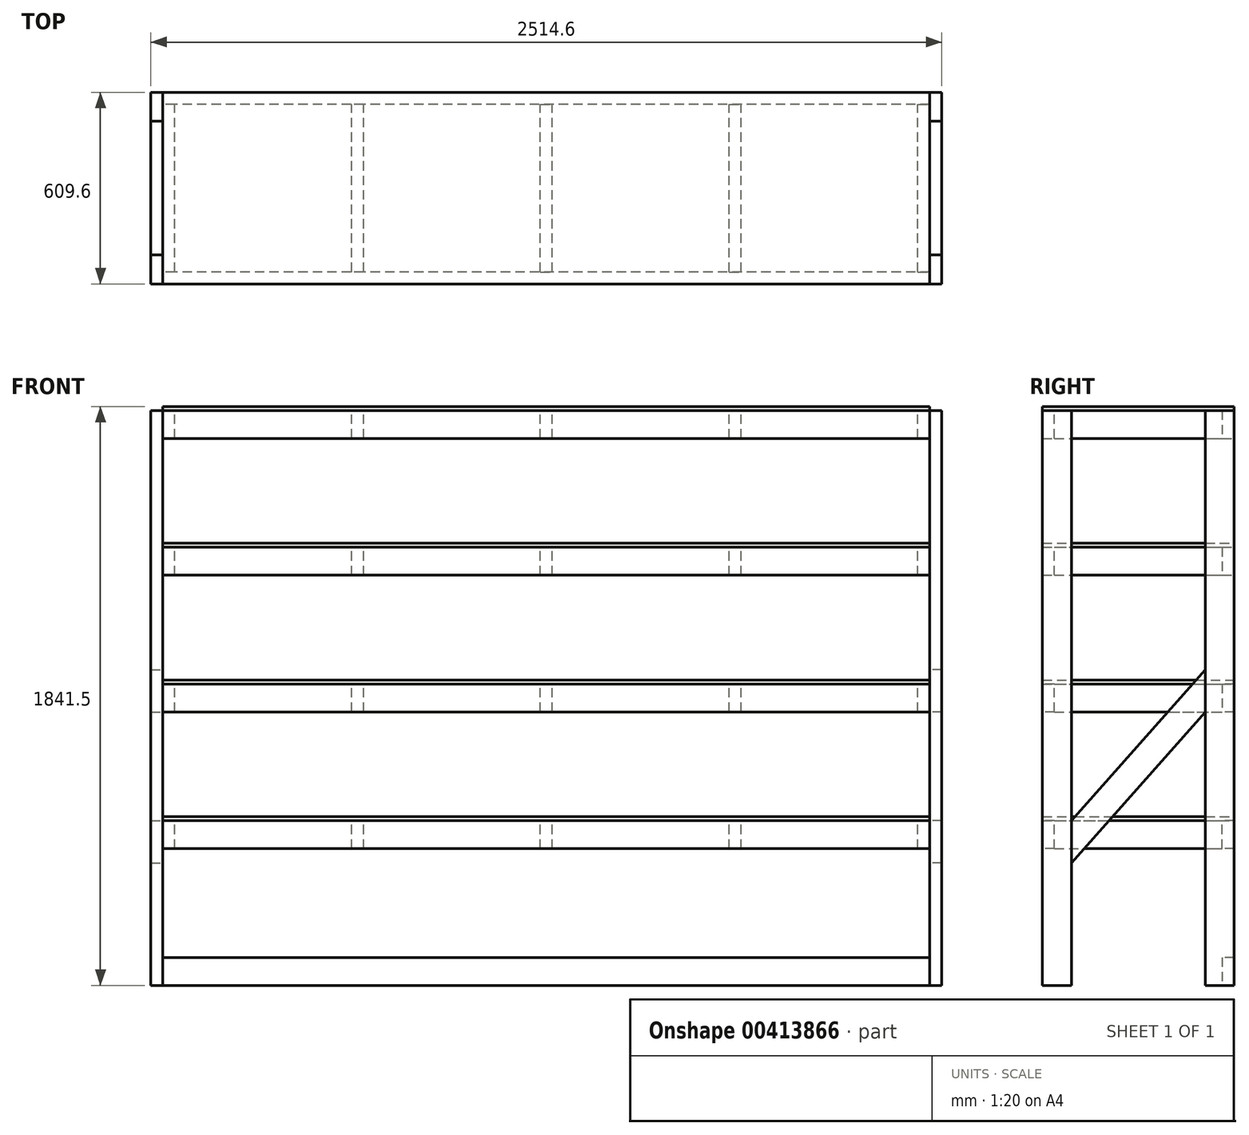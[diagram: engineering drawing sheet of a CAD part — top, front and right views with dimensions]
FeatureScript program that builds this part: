
annotation { "Feature Type Name" : "Feature", "Feature Type Description" : "" }
export const myFeature = defineFeature(function(context is Context, id is Id, definition is map)
    precondition{}
    {
        {
            var Q0;
            Q0=qCreatedBy(makeId("Top.planeOp"),FACE);
            var sketch = newSketch(context, id + "F0", { "sketchPlane" : qUnion([Q0])});
            skLineSegment(sketch, "E0.bottom", {"start": v(1219.2, 304.8) * mm, "end": v(-1219.2, 304.8) * mm, "construction": true});
            skLineSegment(sketch, "E0.top", {"start": v(1219.2, -304.8) * mm, "end": v(-1219.2, -304.8) * mm, "construction": true});
            skLineSegment(sketch, "E0.left", {"start": v(1219.2, 304.8) * mm, "end": v(1219.2, -304.8) * mm, "construction": true});
            skLineSegment(sketch, "E0.right", {"start": v(-1219.2, 304.8) * mm, "end": v(-1219.2, -304.8) * mm, "construction": true});
            skPoint(sketch, "E0.middle", {"position": v(0, 0) * mm});
            skSolve(sketch);
        }
        {
            var Q0;
            Q0=qCreatedBy(makeId("Top.planeOp"),FACE);
            var sketch = newSketch(context, id + "F1", { "sketchPlane" : qUnion([Q0])});
            skLineSegment(sketch, "E1.bottom", {"start": v(-1257.3, 304.8) * mm, "end": v(-1219.2, 304.8) * mm});
            skLineSegment(sketch, "E1.top", {"start": v(-1257.3, 212.72) * mm, "end": v(-1219.2, 212.72) * mm});
            skLineSegment(sketch, "E1.left", {"start": v(-1257.3, 304.8) * mm, "end": v(-1257.3, 212.72) * mm});
            skLineSegment(sketch, "E1.right", {"start": v(-1219.2, 304.8) * mm, "end": v(-1219.2, 212.72) * mm});
            skLineSegment(sketch, "E2.bottom", {"start": v(-1257.3, -304.8) * mm, "end": v(-1219.2, -304.8) * mm});
            skLineSegment(sketch, "E2.top", {"start": v(-1257.3, -212.73) * mm, "end": v(-1219.2, -212.73) * mm});
            skLineSegment(sketch, "E2.left", {"start": v(-1257.3, -304.8) * mm, "end": v(-1257.3, -212.73) * mm});
            skLineSegment(sketch, "E2.right", {"start": v(-1219.2, -304.8) * mm, "end": v(-1219.2, -212.73) * mm});
            skLineSegment(sketch, "E3.bottom", {"start": v(1257.3, -304.8) * mm, "end": v(1219.2, -304.8) * mm});
            skLineSegment(sketch, "E3.top", {"start": v(1257.3, -212.73) * mm, "end": v(1219.2, -212.73) * mm});
            skLineSegment(sketch, "E3.left", {"start": v(1257.3, -304.8) * mm, "end": v(1257.3, -212.73) * mm});
            skLineSegment(sketch, "E3.right", {"start": v(1219.2, -304.8) * mm, "end": v(1219.2, -212.73) * mm});
            skLineSegment(sketch, "E4.bottom", {"start": v(1257.3, 304.8) * mm, "end": v(1219.2, 304.8) * mm});
            skLineSegment(sketch, "E4.top", {"start": v(1257.3, 212.72) * mm, "end": v(1219.2, 212.72) * mm});
            skLineSegment(sketch, "E4.left", {"start": v(1257.3, 304.8) * mm, "end": v(1257.3, 212.72) * mm});
            skLineSegment(sketch, "E4.right", {"start": v(1219.2, 304.8) * mm, "end": v(1219.2, 212.72) * mm});
            skSolve(sketch);
        }
        {
            var Q0;
            Q0=makeQuery(id+"F1.imprint","IMPRINT",FACE,{"disambiguationData":[TD([[makeQuery(id+"F1.imprint","IMPRINT",EDGE,{"derivedFrom":sQuery(id+"F1.wireOp",EDGE,"E2.bottom")}),1.0]])]});
            var Q1;
            Q1=makeQuery(id+"F1.imprint","IMPRINT",FACE,{"disambiguationData":[TD([[makeQuery(id+"F1.imprint","IMPRINT",EDGE,{"derivedFrom":sQuery(id+"F1.wireOp",EDGE,"E1.bottom")}),-1.0]])]});
            var Q2;
            Q2=makeQuery(id+"F1.imprint","IMPRINT",FACE,{"disambiguationData":[TD([[makeQuery(id+"F1.imprint","IMPRINT",EDGE,{"derivedFrom":sQuery(id+"F1.wireOp",EDGE,"E3.bottom")}),-1.0]])]});
            var Q3;
            Q3=makeQuery(id+"F1.imprint","IMPRINT",FACE,{"disambiguationData":[TD([[makeQuery(id+"F1.imprint","IMPRINT",EDGE,{"derivedFrom":sQuery(id+"F1.wireOp",EDGE,"E4.bottom")}),1.0]])]});
            extrude(context, id + "F2", {"entities" : qUnion([Q0, Q1, Q2, Q3]), "depth" : 1828.8 * mm});
        }
        {
            var Q0;
            Q0=qCreatedBy(makeId("Right.planeOp"),FACE);
            var sketch = newSketch(context, id + "F3", { "sketchPlane" : qUnion([Q0])});
            skLineSegment(sketch, "E5.bottom", {"start": v(266.7, 1828.8) * mm, "end": v(304.8, 1828.8) * mm});
            skLineSegment(sketch, "E5.top", {"start": v(266.7, 1739.9) * mm, "end": v(304.8, 1739.9) * mm});
            skLineSegment(sketch, "E5.left", {"start": v(266.7, 1828.8) * mm, "end": v(266.7, 1739.9) * mm});
            skLineSegment(sketch, "E5.right", {"start": v(304.8, 1828.8) * mm, "end": v(304.8, 1739.9) * mm});
            skLineSegment(sketch, "E6.bottom", {"start": v(266.7, 1393.83) * mm, "end": v(304.8, 1393.83) * mm});
            skLineSegment(sketch, "E6.top", {"start": v(266.7, 1304.93) * mm, "end": v(304.8, 1304.93) * mm});
            skLineSegment(sketch, "E6.left", {"start": v(266.7, 1393.83) * mm, "end": v(266.7, 1304.93) * mm});
            skLineSegment(sketch, "E6.right", {"start": v(304.8, 1393.83) * mm, "end": v(304.8, 1304.93) * mm});
            skLineSegment(sketch, "E7.bottom", {"start": v(304.8, 958.85) * mm, "end": v(266.7, 958.85) * mm});
            skLineSegment(sketch, "E7.top", {"start": v(304.8, 869.95) * mm, "end": v(266.7, 869.95) * mm});
            skLineSegment(sketch, "E7.left", {"start": v(304.8, 958.85) * mm, "end": v(304.8, 869.95) * mm});
            skLineSegment(sketch, "E7.right", {"start": v(266.7, 958.85) * mm, "end": v(266.7, 869.95) * mm});
            skLineSegment(sketch, "E8.bottom", {"start": v(304.8, 523.87) * mm, "end": v(266.7, 523.87) * mm});
            skLineSegment(sketch, "E8.top", {"start": v(304.8, 434.98) * mm, "end": v(266.7, 434.98) * mm});
            skLineSegment(sketch, "E8.left", {"start": v(304.8, 523.87) * mm, "end": v(304.8, 434.98) * mm});
            skLineSegment(sketch, "E8.right", {"start": v(266.7, 523.88) * mm, "end": v(266.7, 434.98) * mm});
            skLineSegment(sketch, "E9.bottom", {"start": v(304.8, 88.9) * mm, "end": v(266.7, 88.9) * mm});
            skLineSegment(sketch, "E9.top", {"start": v(304.8, 0) * mm, "end": v(266.7, 0) * mm});
            skLineSegment(sketch, "E9.left", {"start": v(304.8, 88.9) * mm, "end": v(304.8, 0) * mm});
            skLineSegment(sketch, "E9.right", {"start": v(266.7, 88.9) * mm, "end": v(266.7, 0) * mm});
            skLineSegment(sketch, "E10", {"start": v(266.7, 1739.9) * mm, "end": v(266.7, 1393.83) * mm, "construction": true});
            skLineSegment(sketch, "E11", {"start": v(266.7, 1304.93) * mm, "end": v(266.7, 958.85) * mm, "construction": true});
            skLineSegment(sketch, "E12", {"start": v(266.7, 869.95) * mm, "end": v(266.7, 523.87) * mm, "construction": true});
            skLineSegment(sketch, "E13", {"start": v(266.7, 434.98) * mm, "end": v(266.7, 88.9) * mm, "construction": true});
            skLineSegment(sketch, "E14.MirrorCS", {"start": v(-266.7, 1828.8) * mm, "end": v(-304.8, 1828.8) * mm});
            skLineSegment(sketch, "E15.MirrorCS", {"start": v(-266.7, 1739.9) * mm, "end": v(-304.8, 1739.9) * mm});
            skLineSegment(sketch, "E16.MirrorCS", {"start": v(-304.8, 434.98) * mm, "end": v(-266.7, 434.98) * mm});
            skLineSegment(sketch, "E17.MirrorCS", {"start": v(-304.8, 523.87) * mm, "end": v(-266.7, 523.87) * mm});
            skLineSegment(sketch, "E18.MirrorCS", {"start": v(-266.7, 1304.93) * mm, "end": v(-304.8, 1304.93) * mm});
            skLineSegment(sketch, "E19.MirrorCS", {"start": v(-266.7, 1393.83) * mm, "end": v(-304.8, 1393.83) * mm});
            skLineSegment(sketch, "E20.MirrorCS", {"start": v(-304.8, 958.85) * mm, "end": v(-266.7, 958.85) * mm});
            skLineSegment(sketch, "E21.MirrorCS", {"start": v(-304.8, 869.95) * mm, "end": v(-266.7, 869.95) * mm});
            skLineSegment(sketch, "E22.MirrorCS", {"start": v(-266.7, 523.88) * mm, "end": v(-266.7, 434.98) * mm});
            skLineSegment(sketch, "E23.MirrorCS", {"start": v(-266.7, 1828.8) * mm, "end": v(-266.7, 1739.9) * mm});
            skLineSegment(sketch, "E24.MirrorCS", {"start": v(-304.8, 523.87) * mm, "end": v(-304.8, 434.98) * mm});
            skLineSegment(sketch, "E25.MirrorCS", {"start": v(-266.7, 1304.93) * mm, "end": v(-266.7, 958.85) * mm, "construction": true});
            skLineSegment(sketch, "E26.MirrorCS", {"start": v(-266.7, 1393.83) * mm, "end": v(-266.7, 1304.93) * mm});
            skLineSegment(sketch, "E27.MirrorCS", {"start": v(-266.7, 958.85) * mm, "end": v(-266.7, 869.95) * mm});
            skLineSegment(sketch, "E28.MirrorCS", {"start": v(-266.7, 1739.9) * mm, "end": v(-266.7, 1393.83) * mm, "construction": true});
            skLineSegment(sketch, "E29.MirrorCS", {"start": v(-304.8, 958.85) * mm, "end": v(-304.8, 869.95) * mm});
            skLineSegment(sketch, "E30.MirrorCS", {"start": v(-266.7, 869.95) * mm, "end": v(-266.7, 523.87) * mm, "construction": true});
            skLineSegment(sketch, "E31.MirrorCS", {"start": v(-304.8, 1393.83) * mm, "end": v(-304.8, 1304.93) * mm});
            skLineSegment(sketch, "E32.MirrorCS", {"start": v(-304.8, 1828.8) * mm, "end": v(-304.8, 1739.9) * mm});
            skSolve(sketch);
        }
        {
            var Q0;
            Q0 = qSketchRegion(id + "F3", true);
            extrude(context, id + "F4", {"entities" : qUnion([Q0]), "endBound" : BoundingType.UP_TO_NEXT, "depth" : 25.4 * mm, "hasSecondDirection" : true, "secondDirectionBound" : SecondDirectionBoundingType.UP_TO_NEXT, "secondDirectionOppositeDirection" : true, "secondDirectionDepth" : 25.4 * mm});
        }
        {
            var Q0;
            Q0=qCreatedBy(makeId("Front.planeOp"),FACE);
            var sketch = newSketch(context, id + "F5", { "sketchPlane" : qUnion([Q0])});
            skLineSegment(sketch, "E33.bottom", {"start": v(-1219.2, 958.85) * mm, "end": v(-1181.1, 958.85) * mm});
            skLineSegment(sketch, "E33.top", {"start": v(-1219.2, 869.95) * mm, "end": v(-1181.1, 869.95) * mm});
            skLineSegment(sketch, "E33.left", {"start": v(-1219.2, 958.85) * mm, "end": v(-1219.2, 869.95) * mm});
            skLineSegment(sketch, "E33.right", {"start": v(-1181.1, 958.85) * mm, "end": v(-1181.1, 869.95) * mm});
            skLineSegment(sketch, "E34.bottom", {"start": v(-1219.2, 1393.83) * mm, "end": v(-1181.1, 1393.83) * mm});
            skLineSegment(sketch, "E34.top", {"start": v(-1219.2, 1304.93) * mm, "end": v(-1181.1, 1304.93) * mm});
            skLineSegment(sketch, "E34.left", {"start": v(-1219.2, 1393.83) * mm, "end": v(-1219.2, 1304.93) * mm});
            skLineSegment(sketch, "E34.right", {"start": v(-1181.1, 1393.83) * mm, "end": v(-1181.1, 1304.93) * mm});
            skLineSegment(sketch, "E35.bottom", {"start": v(-1219.2, 1828.8) * mm, "end": v(-1181.1, 1828.8) * mm});
            skLineSegment(sketch, "E35.top", {"start": v(-1219.2, 1739.9) * mm, "end": v(-1181.1, 1739.9) * mm});
            skLineSegment(sketch, "E35.left", {"start": v(-1219.2, 1828.8) * mm, "end": v(-1219.2, 1739.9) * mm});
            skLineSegment(sketch, "E35.right", {"start": v(-1181.1, 1828.8) * mm, "end": v(-1181.1, 1739.9) * mm});
            skLineSegment(sketch, "E36.bottom", {"start": v(-1219.2, 523.87) * mm, "end": v(-1181.1, 523.87) * mm});
            skLineSegment(sketch, "E36.top", {"start": v(-1219.2, 434.97) * mm, "end": v(-1181.1, 434.97) * mm});
            skLineSegment(sketch, "E36.left", {"start": v(-1219.2, 523.87) * mm, "end": v(-1219.2, 434.97) * mm});
            skLineSegment(sketch, "E36.right", {"start": v(-1181.1, 523.87) * mm, "end": v(-1181.1, 434.97) * mm});
            skLineSegment(sketch, "E37.bottom", {"start": v(-619.13, 1828.8) * mm, "end": v(-581.02, 1828.8) * mm});
            skLineSegment(sketch, "E37.top", {"start": v(-619.13, 1739.9) * mm, "end": v(-581.02, 1739.9) * mm});
            skLineSegment(sketch, "E37.left", {"start": v(-619.13, 1828.8) * mm, "end": v(-619.13, 1739.9) * mm});
            skLineSegment(sketch, "E37.right", {"start": v(-581.02, 1828.8) * mm, "end": v(-581.02, 1739.9) * mm});
            skLineSegment(sketch, "E38.bottom", {"start": v(-619.13, 1393.83) * mm, "end": v(-581.02, 1393.83) * mm});
            skLineSegment(sketch, "E38.top", {"start": v(-619.13, 1304.93) * mm, "end": v(-581.02, 1304.93) * mm});
            skLineSegment(sketch, "E38.left", {"start": v(-619.13, 1393.83) * mm, "end": v(-619.13, 1304.93) * mm});
            skLineSegment(sketch, "E38.right", {"start": v(-581.02, 1393.83) * mm, "end": v(-581.02, 1304.93) * mm});
            skLineSegment(sketch, "E39.bottom", {"start": v(-619.13, 958.85) * mm, "end": v(-581.02, 958.85) * mm});
            skLineSegment(sketch, "E39.top", {"start": v(-619.13, 869.95) * mm, "end": v(-581.02, 869.95) * mm});
            skLineSegment(sketch, "E39.left", {"start": v(-619.13, 958.85) * mm, "end": v(-619.13, 869.95) * mm});
            skLineSegment(sketch, "E39.right", {"start": v(-581.02, 958.85) * mm, "end": v(-581.02, 869.95) * mm});
            skLineSegment(sketch, "E40.bottom", {"start": v(-619.12, 523.87) * mm, "end": v(-581.02, 523.87) * mm});
            skLineSegment(sketch, "E40.top", {"start": v(-619.13, 434.97) * mm, "end": v(-581.02, 434.97) * mm});
            skLineSegment(sketch, "E40.left", {"start": v(-619.12, 523.87) * mm, "end": v(-619.12, 434.97) * mm});
            skLineSegment(sketch, "E40.right", {"start": v(-581.02, 523.88) * mm, "end": v(-581.02, 434.97) * mm});
            skLineSegment(sketch, "E41", {"start": v(-1181.1, 1828.8) * mm, "end": v(-619.13, 1828.8) * mm, "construction": true});
            skLineSegment(sketch, "E42", {"start": v(-1181.1, 1393.83) * mm, "end": v(-619.13, 1393.83) * mm, "construction": true});
            skLineSegment(sketch, "E43", {"start": v(-1181.1, 958.85) * mm, "end": v(-619.13, 958.85) * mm, "construction": true});
            skLineSegment(sketch, "E44", {"start": v(-1181.1, 523.87) * mm, "end": v(-619.12, 523.87) * mm, "construction": true});
            skLineSegment(sketch, "E45", {"start": v(0, 0) * mm, "end": v(0, 1828.8) * mm, "construction": true});
            skLineSegment(sketch, "E46.bottom", {"start": v(0, 1828.8) * mm, "end": v(-19.05, 1828.8) * mm});
            skLineSegment(sketch, "E46.top", {"start": v(0, 1739.9) * mm, "end": v(-19.05, 1739.9) * mm});
            skLineSegment(sketch, "E46.right", {"start": v(-19.05, 1828.8) * mm, "end": v(-19.05, 1739.9) * mm});
            skLineSegment(sketch, "E47.bottom", {"start": v(0, 1393.83) * mm, "end": v(-19.05, 1393.83) * mm});
            skLineSegment(sketch, "E47.top", {"start": v(0, 1304.93) * mm, "end": v(-19.05, 1304.93) * mm});
            skLineSegment(sketch, "E47.right", {"start": v(-19.05, 1393.83) * mm, "end": v(-19.05, 1304.93) * mm});
            skLineSegment(sketch, "E48.bottom", {"start": v(0, 958.85) * mm, "end": v(-19.05, 958.85) * mm});
            skLineSegment(sketch, "E48.top", {"start": v(0, 869.95) * mm, "end": v(-19.05, 869.95) * mm});
            skLineSegment(sketch, "E48.right", {"start": v(-19.05, 958.85) * mm, "end": v(-19.05, 869.95) * mm});
            skLineSegment(sketch, "E49.bottom", {"start": v(0, 523.87) * mm, "end": v(-19.05, 523.87) * mm});
            skLineSegment(sketch, "E49.top", {"start": v(0, 434.98) * mm, "end": v(-19.05, 434.98) * mm});
            skLineSegment(sketch, "E49.right", {"start": v(-19.05, 523.87) * mm, "end": v(-19.05, 434.98) * mm});
            skLineSegment(sketch, "E50", {"start": v(-581.02, 1828.8) * mm, "end": v(-19.05, 1828.8) * mm, "construction": true});
            skLineSegment(sketch, "E51.MirrorCS", {"start": v(0, 1739.9) * mm, "end": v(19.05, 1739.9) * mm});
            skLineSegment(sketch, "E52.MirrorCS", {"start": v(0, 1304.93) * mm, "end": v(19.05, 1304.93) * mm});
            skLineSegment(sketch, "E53.MirrorCS", {"start": v(0, 869.95) * mm, "end": v(19.05, 869.95) * mm});
            skLineSegment(sketch, "E54.MirrorCS", {"start": v(619.13, 1828.8) * mm, "end": v(581.02, 1828.8) * mm});
            skLineSegment(sketch, "E55.MirrorCS", {"start": v(0, 1828.8) * mm, "end": v(19.05, 1828.8) * mm});
            skLineSegment(sketch, "E56.MirrorCS", {"start": v(0, 1393.83) * mm, "end": v(19.05, 1393.83) * mm});
            skLineSegment(sketch, "E57.MirrorCS", {"start": v(619.13, 1304.93) * mm, "end": v(581.02, 1304.93) * mm});
            skLineSegment(sketch, "E58.MirrorCS", {"start": v(619.13, 869.95) * mm, "end": v(581.02, 869.95) * mm});
            skLineSegment(sketch, "E59.MirrorCS", {"start": v(0, 434.98) * mm, "end": v(19.05, 434.98) * mm});
            skLineSegment(sketch, "E60.MirrorCS", {"start": v(1219.2, 1304.93) * mm, "end": v(1181.1, 1304.93) * mm});
            skLineSegment(sketch, "E61.MirrorCS", {"start": v(619.13, 434.97) * mm, "end": v(581.02, 434.97) * mm});
            skLineSegment(sketch, "E62.MirrorCS", {"start": v(1219.2, 869.95) * mm, "end": v(1181.1, 869.95) * mm});
            skLineSegment(sketch, "E63.MirrorCS", {"start": v(1219.2, 434.97) * mm, "end": v(1181.1, 434.97) * mm});
            skLineSegment(sketch, "E64.MirrorCS", {"start": v(619.13, 1739.9) * mm, "end": v(581.02, 1739.9) * mm});
            skLineSegment(sketch, "E65.MirrorCS", {"start": v(619.13, 958.85) * mm, "end": v(581.02, 958.85) * mm});
            skLineSegment(sketch, "E66.MirrorCS", {"start": v(1219.2, 1393.83) * mm, "end": v(1181.1, 1393.83) * mm});
            skLineSegment(sketch, "E67.MirrorCS", {"start": v(0, 958.85) * mm, "end": v(19.05, 958.85) * mm});
            skLineSegment(sketch, "E68.MirrorCS", {"start": v(1219.2, 523.87) * mm, "end": v(1181.1, 523.87) * mm});
            skLineSegment(sketch, "E69.MirrorCS", {"start": v(1219.2, 958.85) * mm, "end": v(1181.1, 958.85) * mm});
            skLineSegment(sketch, "E70.MirrorCS", {"start": v(619.13, 1393.83) * mm, "end": v(581.02, 1393.83) * mm});
            skLineSegment(sketch, "E71.MirrorCS", {"start": v(1219.2, 1739.9) * mm, "end": v(1181.1, 1739.9) * mm});
            skLineSegment(sketch, "E72.MirrorCS", {"start": v(0, 523.87) * mm, "end": v(19.05, 523.87) * mm});
            skLineSegment(sketch, "E73.MirrorCS", {"start": v(1219.2, 1828.8) * mm, "end": v(1181.1, 1828.8) * mm});
            skLineSegment(sketch, "E74.MirrorCS", {"start": v(619.12, 523.87) * mm, "end": v(581.02, 523.87) * mm});
            skLineSegment(sketch, "E75.MirrorCS", {"start": v(19.05, 958.85) * mm, "end": v(19.05, 869.95) * mm});
            skLineSegment(sketch, "E76.MirrorCS", {"start": v(581.02, 523.88) * mm, "end": v(581.02, 434.97) * mm});
            skLineSegment(sketch, "E77.MirrorCS", {"start": v(581.02, 1828.8) * mm, "end": v(581.02, 1739.9) * mm});
            skLineSegment(sketch, "E78.MirrorCS", {"start": v(619.12, 523.87) * mm, "end": v(619.12, 434.97) * mm});
            skLineSegment(sketch, "E79.MirrorCS", {"start": v(1181.1, 523.87) * mm, "end": v(619.12, 523.87) * mm, "construction": true});
            skLineSegment(sketch, "E80.MirrorCS", {"start": v(19.05, 1393.83) * mm, "end": v(19.05, 1304.93) * mm});
            skLineSegment(sketch, "E81.MirrorCS", {"start": v(619.13, 1828.8) * mm, "end": v(619.13, 1739.9) * mm});
            skLineSegment(sketch, "E82.MirrorCS", {"start": v(1219.2, 1393.83) * mm, "end": v(1219.2, 1304.93) * mm});
            skLineSegment(sketch, "E83.MirrorCS", {"start": v(1181.1, 958.85) * mm, "end": v(1181.1, 869.95) * mm});
            skLineSegment(sketch, "E84.MirrorCS", {"start": v(1181.1, 958.85) * mm, "end": v(619.13, 958.85) * mm, "construction": true});
            skLineSegment(sketch, "E85.MirrorCS", {"start": v(19.05, 523.87) * mm, "end": v(19.05, 434.98) * mm});
            skLineSegment(sketch, "E86.MirrorCS", {"start": v(1219.2, 1828.8) * mm, "end": v(1219.2, 1739.9) * mm});
            skLineSegment(sketch, "E87.MirrorCS", {"start": v(619.13, 1393.83) * mm, "end": v(619.13, 1304.93) * mm});
            skLineSegment(sketch, "E88.MirrorCS", {"start": v(1181.1, 1828.8) * mm, "end": v(1181.1, 1739.9) * mm});
            skLineSegment(sketch, "E89.MirrorCS", {"start": v(619.12, 958.85) * mm, "end": v(619.12, 869.95) * mm});
            skLineSegment(sketch, "E90.MirrorCS", {"start": v(581.02, 958.85) * mm, "end": v(581.02, 869.95) * mm});
            skLineSegment(sketch, "E91.MirrorCS", {"start": v(1181.1, 523.87) * mm, "end": v(1181.1, 434.97) * mm});
            skLineSegment(sketch, "E92.MirrorCS", {"start": v(581.02, 1393.83) * mm, "end": v(581.02, 1304.93) * mm});
            skLineSegment(sketch, "E93.MirrorCS", {"start": v(581.02, 1828.8) * mm, "end": v(19.05, 1828.8) * mm, "construction": true});
            skLineSegment(sketch, "E94.MirrorCS", {"start": v(1181.1, 1393.83) * mm, "end": v(1181.1, 1304.93) * mm});
            skLineSegment(sketch, "E95.MirrorCS", {"start": v(1219.2, 523.87) * mm, "end": v(1219.2, 434.97) * mm});
            skLineSegment(sketch, "E96.MirrorCS", {"start": v(19.05, 1828.8) * mm, "end": v(19.05, 1739.9) * mm});
            skLineSegment(sketch, "E97.MirrorCS", {"start": v(1181.1, 1828.8) * mm, "end": v(619.13, 1828.8) * mm, "construction": true});
            skLineSegment(sketch, "E98.MirrorCS", {"start": v(1219.2, 958.85) * mm, "end": v(1219.2, 869.95) * mm});
            skLineSegment(sketch, "E99.MirrorCS", {"start": v(1181.1, 1393.83) * mm, "end": v(619.13, 1393.83) * mm, "construction": true});
            skLineSegment(sketch, "E100", {"start": v(-581.02, 523.87) * mm, "end": v(-19.05, 523.87) * mm, "construction": true});
            skLineSegment(sketch, "E101", {"start": v(-581.02, 958.85) * mm, "end": v(-19.05, 958.85) * mm, "construction": true});
            skLineSegment(sketch, "E102", {"start": v(-581.02, 1393.83) * mm, "end": v(-19.05, 1393.83) * mm, "construction": true});
            skSolve(sketch);
        }
        {
            var Q0;
            Q0 = qSketchRegion(id + "F5", true);
            extrude(context, id + "F6", {"entities" : qUnion([Q0]), "endBound" : BoundingType.UP_TO_NEXT, "depth" : 25.4 * mm, "hasSecondDirection" : true, "secondDirectionBound" : SecondDirectionBoundingType.UP_TO_NEXT, "secondDirectionOppositeDirection" : true, "secondDirectionDepth" : 25.4 * mm});
        }
        {
            var Q0;
            Q0=qCreatedBy(makeId("Front.planeOp"),FACE);
            var sketch = newSketch(context, id + "F7", { "sketchPlane" : qUnion([Q0])});
            skLineSegment(sketch, "E103.bottom", {"start": v(-1219.2, 523.87) * mm, "end": v(1219.2, 523.87) * mm});
            skLineSegment(sketch, "E103.top", {"start": v(-1219.2, 536.58) * mm, "end": v(1219.2, 536.58) * mm});
            skLineSegment(sketch, "E103.left", {"start": v(-1219.2, 523.87) * mm, "end": v(-1219.2, 536.58) * mm});
            skLineSegment(sketch, "E103.right", {"start": v(1219.2, 523.87) * mm, "end": v(1219.2, 536.58) * mm});
            skLineSegment(sketch, "E104.bottom", {"start": v(-1219.2, 958.85) * mm, "end": v(1219.2, 958.85) * mm});
            skLineSegment(sketch, "E104.top", {"start": v(-1219.2, 971.55) * mm, "end": v(1219.2, 971.55) * mm});
            skLineSegment(sketch, "E104.left", {"start": v(-1219.2, 958.85) * mm, "end": v(-1219.2, 971.55) * mm});
            skLineSegment(sketch, "E104.right", {"start": v(1219.2, 958.85) * mm, "end": v(1219.2, 971.55) * mm});
            skLineSegment(sketch, "E105.bottom", {"start": v(-1219.2, 1393.83) * mm, "end": v(1219.2, 1393.83) * mm});
            skLineSegment(sketch, "E105.top", {"start": v(-1219.2, 1406.53) * mm, "end": v(1219.2, 1406.53) * mm});
            skLineSegment(sketch, "E105.left", {"start": v(-1219.2, 1393.83) * mm, "end": v(-1219.2, 1406.53) * mm});
            skLineSegment(sketch, "E105.right", {"start": v(1219.2, 1393.83) * mm, "end": v(1219.2, 1406.53) * mm});
            skLineSegment(sketch, "E106.bottom", {"start": v(-1219.2, 1828.8) * mm, "end": v(1219.2, 1828.8) * mm});
            skLineSegment(sketch, "E106.top", {"start": v(-1219.2, 1841.5) * mm, "end": v(1219.2, 1841.5) * mm});
            skLineSegment(sketch, "E106.left", {"start": v(-1219.2, 1828.8) * mm, "end": v(-1219.2, 1841.5) * mm});
            skLineSegment(sketch, "E106.right", {"start": v(1219.2, 1828.8) * mm, "end": v(1219.2, 1841.5) * mm});
            skSolve(sketch);
        }
        {
            var Q0;
            Q0 = qSketchRegion(id + "F7", true);
            var Q1;
            Q1=makeQuery(id+"F4.opExtrude","SWEPT_FACE",FACE,{"disambiguationData":[OSD([sQuery(id+"F3.wireOp",EDGE,"E32.MirrorCS")])]});
            var Q2;
            Q2=makeQuery(id+"F4.opExtrude","SWEPT_FACE",FACE,{"disambiguationData":[OSD([sQuery(id+"F3.wireOp",EDGE,"E5.right")])]});
            extrude(context, id + "F8", {"entities" : qUnion([Q0]), "endBound" : BoundingType.UP_TO_SURFACE, "endBoundEntityFace" : qUnion([Q1]), "depth" : 25.4 * mm, "hasSecondDirection" : true, "secondDirectionBound" : SecondDirectionBoundingType.UP_TO_SURFACE, "secondDirectionOppositeDirection" : true, "secondDirectionBoundEntityFace" : qUnion([Q2]), "secondDirectionDepth" : 25.4 * mm});
        }
        {
            var Q0;
            Q0=makeQuery(id+"F6.opExtrude","SWEPT_FACE",FACE,{"disambiguationData":[OSD([sQuery(id+"F5.wireOp",EDGE,"E98.MirrorCS")])]});
            var sketch = newSketch(context, id + "F9", { "sketchPlane" : qUnion([Q0])});
            skLineSegment(sketch, "E107", {"start": v(-212.73, 389.83) * mm, "end": v(212.72, 869.95) * mm});
            skLineSegment(sketch, "E108", {"start": v(212.72, 869.95) * mm, "end": v(212.72, 1004) * mm});
            skLineSegment(sketch, "E109", {"start": v(212.72, 1004) * mm, "end": v(-212.72, 523.88) * mm});
            skLineSegment(sketch, "E110", {"start": v(-212.73, 523.88) * mm, "end": v(-212.73, 389.83) * mm});
            skSolve(sketch);
        }
        {
            var Q0;
            Q0 = qSketchRegion(id + "F9", true);
            extrude(context, id + "F10", {"entities" : qUnion([Q0]), "depth" : 38.1 * mm});
        }
        {
            var Q0;
            Q0=makeQuery(id+"F6.opExtrude","SWEPT_FACE",FACE,{"disambiguationData":[OSD([sQuery(id+"F5.wireOp",EDGE,"E36.left")])]});
            var sketch = newSketch(context, id + "F11", { "sketchPlane" : qUnion([Q0])});
            skLineSegment(sketch, "E111", {"start": v(-212.72, 1004) * mm, "end": v(-212.72, 869.95) * mm});
            skLineSegment(sketch, "E112", {"start": v(-212.72, 869.95) * mm, "end": v(212.73, 389.83) * mm});
            skLineSegment(sketch, "E113", {"start": v(212.73, 389.83) * mm, "end": v(212.73, 523.87) * mm});
            skLineSegment(sketch, "E114", {"start": v(212.73, 523.87) * mm, "end": v(-212.72, 1004) * mm});
            skSolve(sketch);
        }
        {
            var Q0;
            Q0 = qSketchRegion(id + "F11", true);
            extrude(context, id + "F12", {"entities" : qUnion([Q0]), "depth" : 38.1 * mm});
        }
    });
